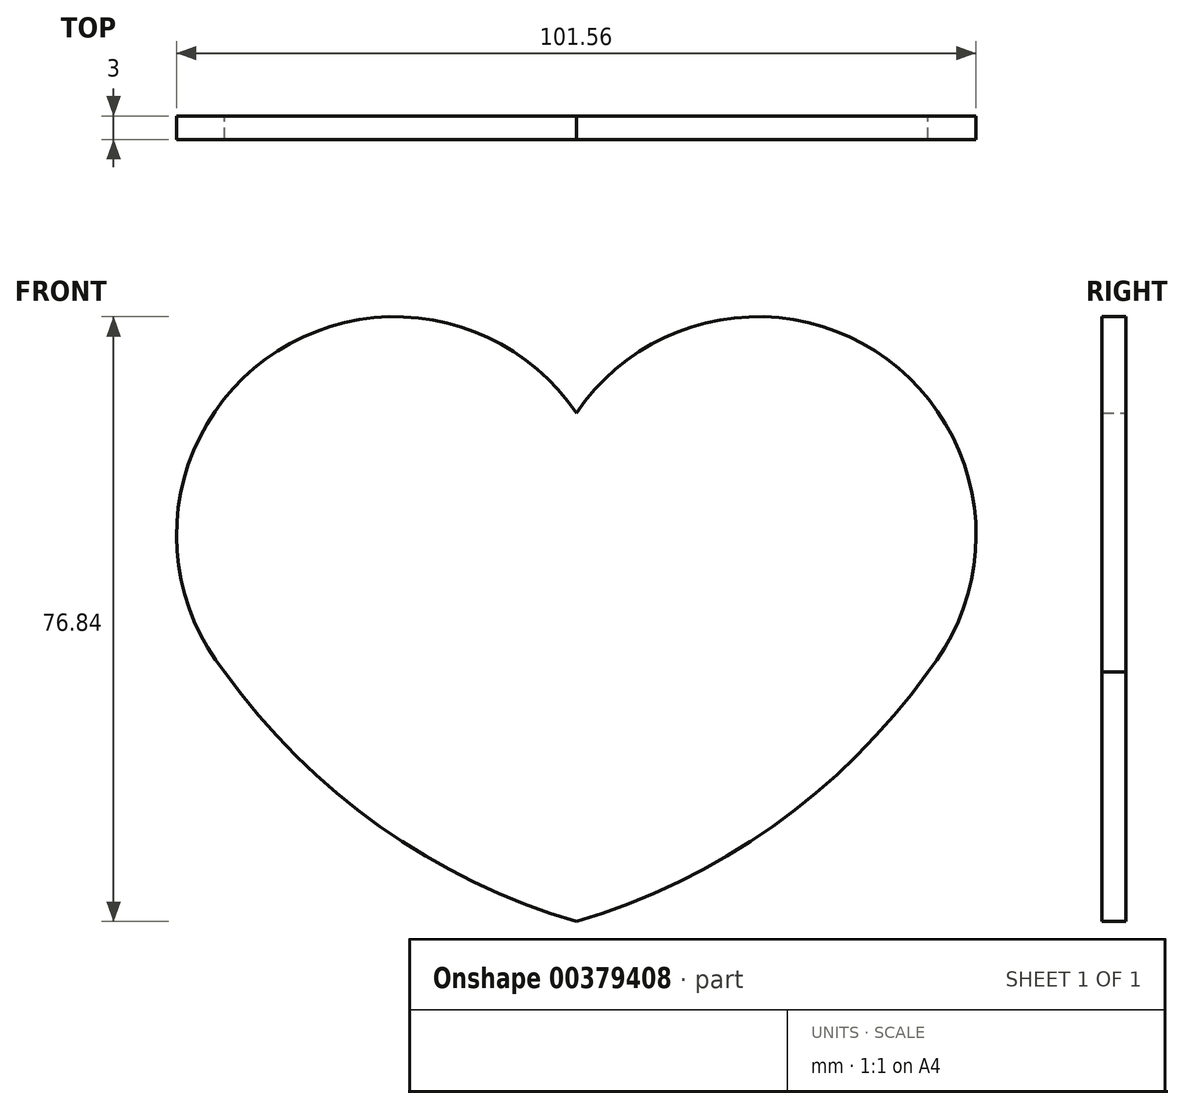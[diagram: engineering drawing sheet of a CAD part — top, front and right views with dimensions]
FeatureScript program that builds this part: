
annotation { "Feature Type Name" : "Feature", "Feature Type Description" : "" }
export const myFeature = defineFeature(function(context is Context, id is Id, definition is map)
    precondition{}
    {
        {
            var Q0;
            Q0=qCreatedBy(makeId("Front.planeOp"),FACE);
            var sketch = newSketch(context, id + "F0", { "sketchPlane" : qUnion([Q0])});
            skArc(sketch, "E0", {"start": v(0, 15.5) * mm, "mid": v(-39.49, 22.35) * mm, "end": v(-44.66, -17.4) * mm});
            skPoint(sketch, "E1", {"position": v(0, -49.08) * mm});
            skArc(sketch, "E2", {"start": v(-44.66, -17.4) * mm, "mid": v(-24.98, -36.97) * mm, "end": v(0, -49.08) * mm});
            skArc(sketch, "E3.MirrorCS", {"start": v(44.66, -17.4) * mm, "mid": v(24.98, -36.97) * mm, "end": v(0, -49.08) * mm});
            skArc(sketch, "E4.MirrorC", {"start": v(0, 15.5) * mm, "mid": v(39.49, 22.35) * mm, "end": v(44.66, -17.4) * mm});
            skSolve(sketch);
        }
        {
            var Q0;
            Q0 = qSketchRegion(id + "F0", true);
            extrude(context, id + "F1", {"entities" : qUnion([Q0]), "depth" : 3 * mm});
        }
    });
